# Revit family: WL218-sw
name_source: partatom
category: Communication Devices
revit_build: Autodesk Revit Architecture 2012 (Build: 20110309_2315(x64)
units: mm (PartAtom-declared; Revit-internal decimal feet)

## types (1)
- WL218-sw
    Apex Offset From Front = 1.183 "
    Default Elevation = 48 "
    Depth = 34.75 "
    Description = Vented Dual 18" Subwoofer
    Enclosure Material = Black Finish
    Grill Extent Height = 19.072 "
    Grill Material = Black Grille
    Grill Width = 43.42 "
    Height = 21.32 "
    Impedance = 4
    Manufacturer = QSC Audio Products, LLC
    Manufacturer URL = www.qscaudio.com
    Model = WL218-sw
    Power Handling = 3000
    Product Documentation Link = http://media.qscaudio.com
    Product Page URL = http://www.qscaudio.com
    Rear Height = 16 "
    Regulatory Compliance = RoHS
    SPL Max = 133
    Sensitivity = 101
    URL = http://www.qscaudio.com
    Weight Dimensional (kg) = 110
    Weight Dimensional (lb) = 244
    Weight Product (kg) = 92.5
    Weight Product (lb) = 204
    Width = 45.92 "

## geometry (parser evidence)
native form markers: Blend x2, Sweep x1
no freeform markers — native parametric forms only
